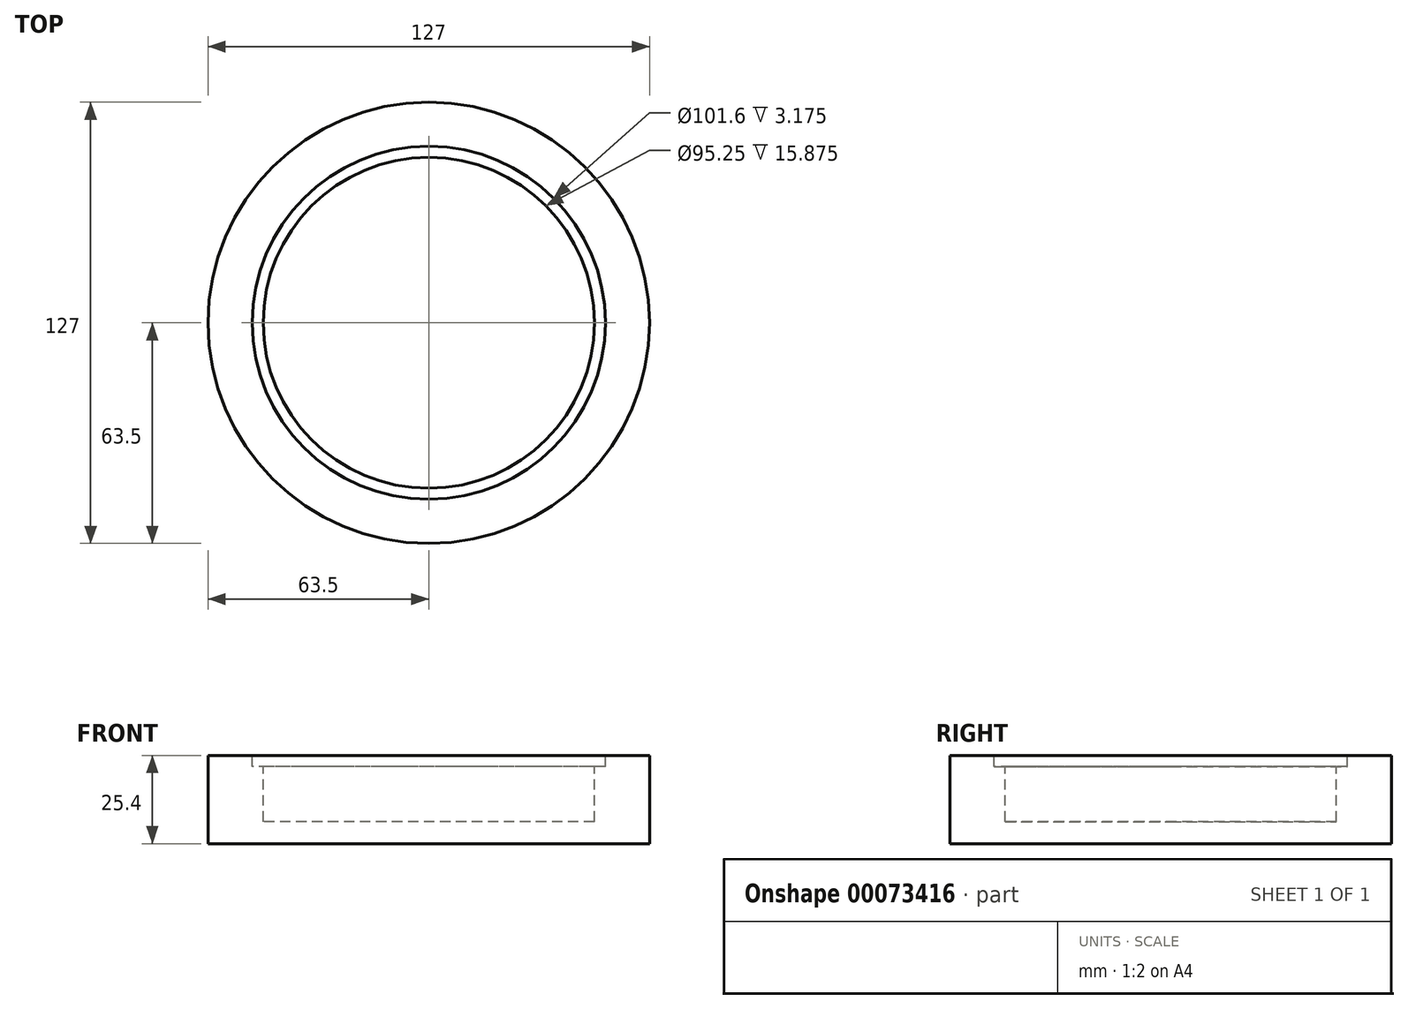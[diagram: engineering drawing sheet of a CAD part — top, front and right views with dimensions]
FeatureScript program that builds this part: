
annotation { "Feature Type Name" : "Feature", "Feature Type Description" : "" }
export const myFeature = defineFeature(function(context is Context, id is Id, definition is map)
    precondition{}
    {
        {
            var Q0;
            Q0=qCreatedBy(makeId("Top.planeOp"),FACE);
            var sketch = newSketch(context, id + "F0", { "sketchPlane" : qUnion([Q0])});
            skCircle(sketch, "E0", {"center": v(0, 0) * mm, "radius": 63.5 * mm});
            skSolve(sketch);
        }
        {
            var Q0;
            Q0=makeQuery(id+"F0.imprint","IMPRINT",FACE,{"disambiguationData":[TD([[makeQuery(id+"F0.imprint","IMPRINT",EDGE,{"derivedFrom":sQuery(id+"F0.wireOp",EDGE,"E0")}),1.0]])]});
            extrude(context, id + "F1", {"entities" : qUnion([Q0]), "depth" : 25.4 * mm});
        }
        {
            var Q0;
            Q0=makeQuery(id+"F1.opExtrude","CAP_FACE",FACE,{"disambiguationData":[OSD([sQuery(id+"F0.wireOp",EDGE,"E0")])],"isStart":false});
            var sketch = newSketch(context, id + "F2", { "sketchPlane" : qUnion([Q0])});
            skCircle(sketch, "E1", {"center": v(0, 0) * mm, "radius": 47.63 * mm});
            skSolve(sketch);
        }
        {
            var Q0;
            Q0=makeQuery(id+"F2.imprint","IMPRINT",FACE,{"disambiguationData":[TD([[makeQuery(id+"F2.imprint","IMPRINT",EDGE,{"derivedFrom":sQuery(id+"F2.wireOp",EDGE,"E1")}),1.0]])]});
            extrude(context, id + "F3", {"entities" : qUnion([Q0]), "operationType" : NewBodyOperationType.REMOVE, "oppositeDirection" : true, "depth" : 19.05 * mm});
        }
        {
            var Q0;
            Q0=makeQuery(id+"F1.opExtrude","CAP_FACE",FACE,{"disambiguationData":[OSD([sQuery(id+"F0.wireOp",EDGE,"E0")])],"isStart":false});
            var sketch = newSketch(context, id + "F4", { "sketchPlane" : qUnion([Q0])});
            skCircle(sketch, "E2", {"center": v(0, 0) * mm, "radius": 50.8 * mm});
            skSolve(sketch);
        }
        {
            var Q0;
            Q0=makeQuery(id+"F4.imprint","IMPRINT",FACE,{"disambiguationData":[TD([[makeQuery(id+"F4.imprint","IMPRINT",EDGE,{"derivedFrom":sQuery(id+"F4.wireOp",EDGE,"E2")}),1.0]])]});
            extrude(context, id + "F5", {"entities" : qUnion([Q0]), "operationType" : NewBodyOperationType.REMOVE, "oppositeDirection" : true, "depth" : 3.17 * mm});
        }
    });
